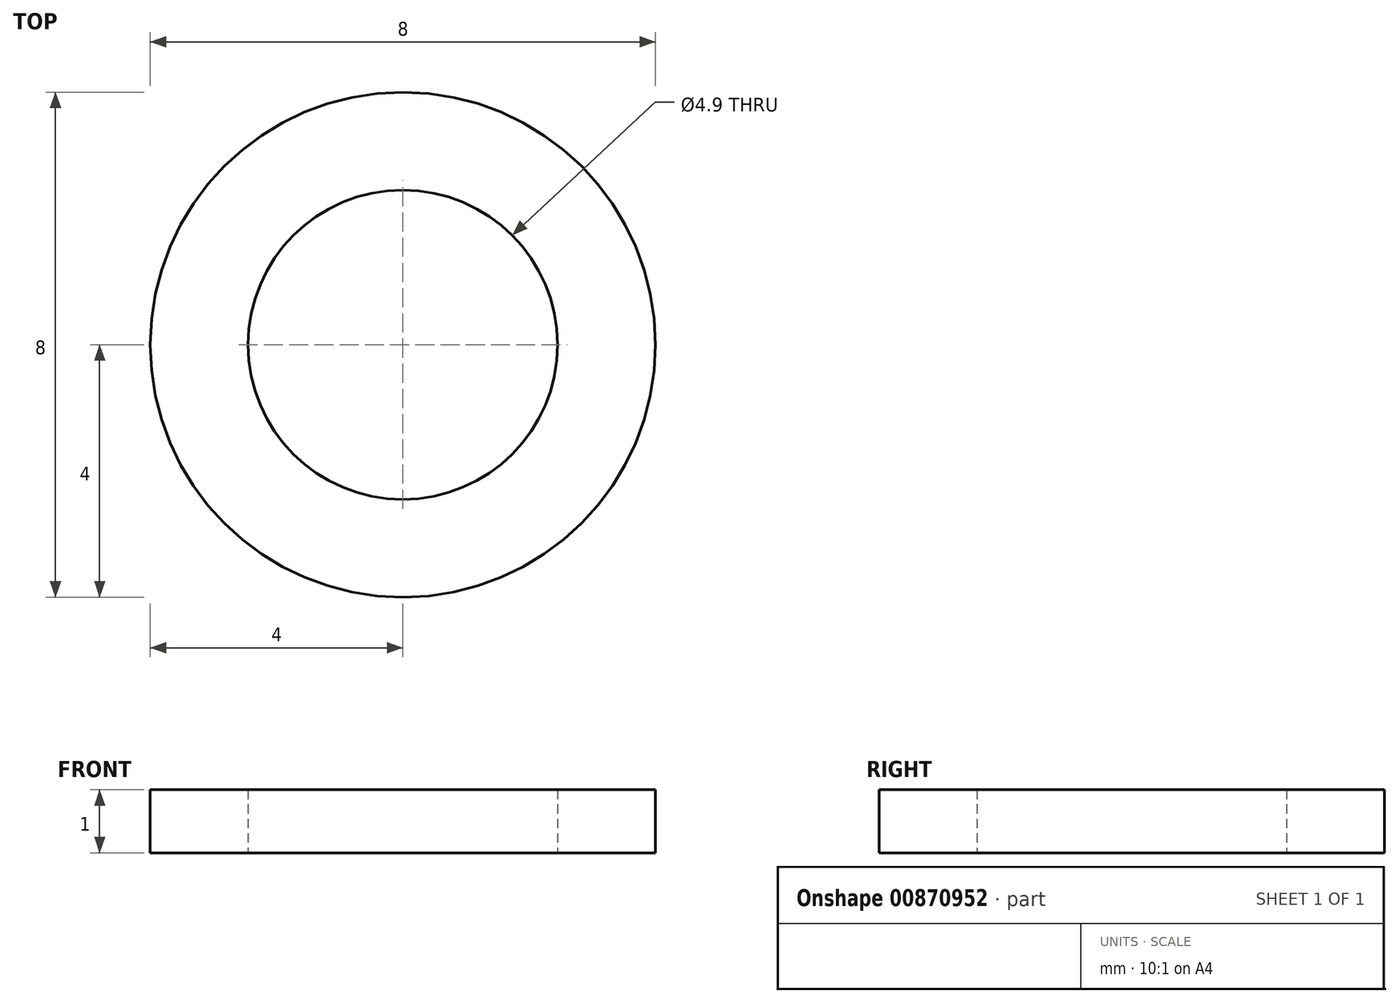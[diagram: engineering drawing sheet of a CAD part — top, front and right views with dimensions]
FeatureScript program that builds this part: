
annotation { "Feature Type Name" : "Feature", "Feature Type Description" : "" }
export const myFeature = defineFeature(function(context is Context, id is Id, definition is map)
    precondition{}
    {
        {
            var Q0;
            Q0=qCreatedBy(makeId("Top.planeOp"),FACE);
            var sketch = newSketch(context, id + "F0", { "sketchPlane" : qUnion([Q0])});
            skCircle(sketch, "E0", {"center": v(0, 0) * mm, "radius": 2.45 * mm});
            skCircle(sketch, "E1", {"center": v(0, 0) * mm, "radius": 4 * mm});
            skSolve(sketch);
        }
        {
            var Q0;
            Q0=makeQuery(id+"F0.imprint","IMPRINT",FACE,{"disambiguationData":[TD([[makeQuery(id+"F0.imprint","IMPRINT",EDGE,{"derivedFrom":sQuery(id+"F0.wireOp",EDGE,"E0")}),-1.0]])]});
            extrude(context, id + "F1", {"entities" : qUnion([Q0]), "depth" : 1 * mm, "offsetDistance" : 25 * mm});
        }
    });
